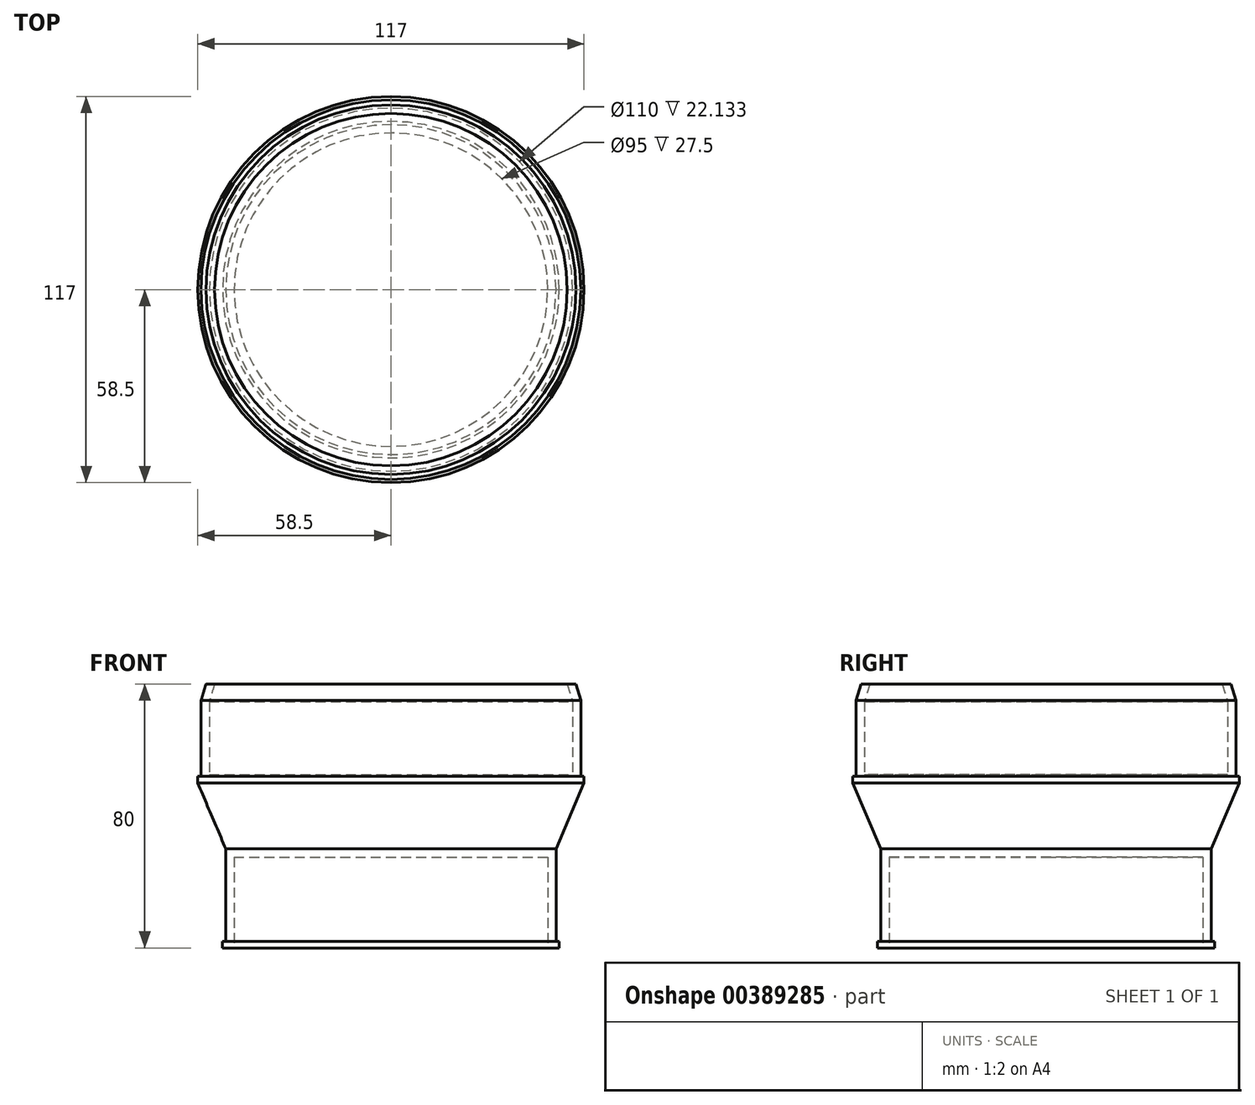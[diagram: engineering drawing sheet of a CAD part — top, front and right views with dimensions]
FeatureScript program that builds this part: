
annotation { "Feature Type Name" : "Feature", "Feature Type Description" : "" }
export const myFeature = defineFeature(function(context is Context, id is Id, definition is map)
    precondition{}
    {
        {
            var Q0;
            Q0=qCreatedBy(makeId("Front.planeOp"),FACE);
            var sketch = newSketch(context, id + "F0", { "sketchPlane" : qUnion([Q0])});
            skLineSegment(sketch, "E0.bottom", {"start": v(0, 0) * mm, "end": v(-57.5, 0) * mm});
            skLineSegment(sketch, "E0.top", {"start": v(0, 30) * mm, "end": v(-56, 30) * mm});
            skLineSegment(sketch, "E0.left", {"start": v(0, 0) * mm, "end": v(0, 30) * mm});
            skLineSegment(sketch, "E0.right", {"start": v(-57.5, 0) * mm, "end": v(-57.5, 25) * mm});
            skLineSegment(sketch, "E1", {"start": v(-56, 30) * mm, "end": v(-57.5, 25) * mm});
            skLineSegment(sketch, "E2", {"start": v(-56, 30) * mm, "end": v(-57.5, 30) * mm, "construction": true});
            skLineSegment(sketch, "E3", {"start": v(-57.5, 25) * mm, "end": v(-57.5, 30) * mm, "construction": true});
            skLineSegment(sketch, "E4.bottom", {"start": v(0, -50) * mm, "end": v(-50, -50) * mm});
            skLineSegment(sketch, "E4.top", {"start": v(0, -20) * mm, "end": v(-50, -20) * mm});
            skLineSegment(sketch, "E4.left", {"start": v(0, -50) * mm, "end": v(0, -20) * mm});
            skLineSegment(sketch, "E4.right", {"start": v(-50, -50) * mm, "end": v(-50, -20) * mm});
            skLineSegment(sketch, "E5.bottom", {"start": v(-50, -50) * mm, "end": v(-51, -50) * mm});
            skLineSegment(sketch, "E5.top", {"start": v(-50, -48) * mm, "end": v(-51, -48) * mm});
            skLineSegment(sketch, "E5.left", {"start": v(-50, -50) * mm, "end": v(-50, -48) * mm});
            skLineSegment(sketch, "E5.right", {"start": v(-51, -50) * mm, "end": v(-51, -48) * mm});
            skLineSegment(sketch, "E6.bottom", {"start": v(-57.5, 0) * mm, "end": v(-58.5, 0) * mm});
            skLineSegment(sketch, "E6.top", {"start": v(-57.5, 2) * mm, "end": v(-58.5, 2) * mm});
            skLineSegment(sketch, "E6.left", {"start": v(-57.5, 0) * mm, "end": v(-57.5, 2) * mm});
            skLineSegment(sketch, "E6.right", {"start": v(-58.5, 0) * mm, "end": v(-58.5, 2) * mm});
            skSolve(sketch);
        }
        {
            var Q0;
            Q0=makeQuery(id+"F0.imprint","IMPRINT",FACE,{"disambiguationData":[TD([[makeQuery(id+"F0.imprint","IMPRINT",EDGE,{"derivedFrom":sQuery(id+"F0.wireOp",EDGE,"E0.bottom")}),-1.0]])]});
            var Q1;
            {var subQ3=sQuery(id+"F0.wireOp",EDGE,"E4.bottom");Q1=makeQuery(id+"F0.imprint","IMPRINT",FACE,{"disambiguationData":[TD([[makeQuery(id+"F0.imprint","IMPRINT",EDGE,{"derivedFrom":subQ3}),-1.0]])]});}
            var Q2;
            {var subQ0=sQuery(id+"F0.wireOp",EDGE,"E5.bottom");Q2=makeQuery(id+"F0.imprint","IMPRINT",FACE,{"disambiguationData":[TD([[makeQuery(id+"F0.imprint","IMPRINT",EDGE,{"derivedFrom":subQ0}),-1.0]])]});}
            var Q3;
            {var subQ0=sQuery(id+"F0.wireOp",EDGE,"E6.bottom");Q3=makeQuery(id+"F0.imprint","IMPRINT",FACE,{"disambiguationData":[TD([[makeQuery(id+"F0.imprint","IMPRINT",EDGE,{"derivedFrom":subQ0}),-1.0]])]});}
            var Q4;
            Q4=sQuery(id+"F0.wireOp",EDGE,"E0.left");
            revolve(context, id + "F1", {"surfaceOperationType" : NewSurfaceOperationType.NEW, "entities" : qUnion([Q0, Q1, Q2, Q3]), "axis" : qUnion([Q4]), "revolveType" : RevolveType.FULL});
        }
        {
            var Q0;
            Q0=makeQuery(id+"F1.opRevolve","SWEPT_FACE",FACE,{"disambiguationData":[OSD([sQuery(id+"F0.wireOp",EDGE,"E0.bottom")])]});
            var Q1;
            Q1=makeQuery(id+"F1.opRevolve","SWEPT_FACE",FACE,{"disambiguationData":[OSD([sQuery(id+"F0.wireOp",EDGE,"E4.top")])]});
            loft(context, id + "F2", {"sheetProfilesArray" : [{ "sheetProfileEntities" : qUnion([Q0]) }, { "sheetProfileEntities" : qUnion([Q1]) }]});
        }
        {
            var Q0;
            Q0=makeQuery(id+"F1.opRevolve","SWEPT_FACE",FACE,{"disambiguationData":[OSD([sQuery(id+"F0.wireOp",EDGE,"E0.top")])]});
            var Q1;
            Q1=makeQuery(id+"F1.opRevolve","SWEPT_FACE",FACE,{"disambiguationData":[OSD([sQuery(id+"F0.wireOp",EDGE,"E4.bottom"),sQuery(id+"F0.wireOp",EDGE,"E5.bottom")])]});
            shell(context, id + "F3", {"entities" : qUnion([Q0, Q1]), "thickness" : 2.5 * mm});
        }
    });
